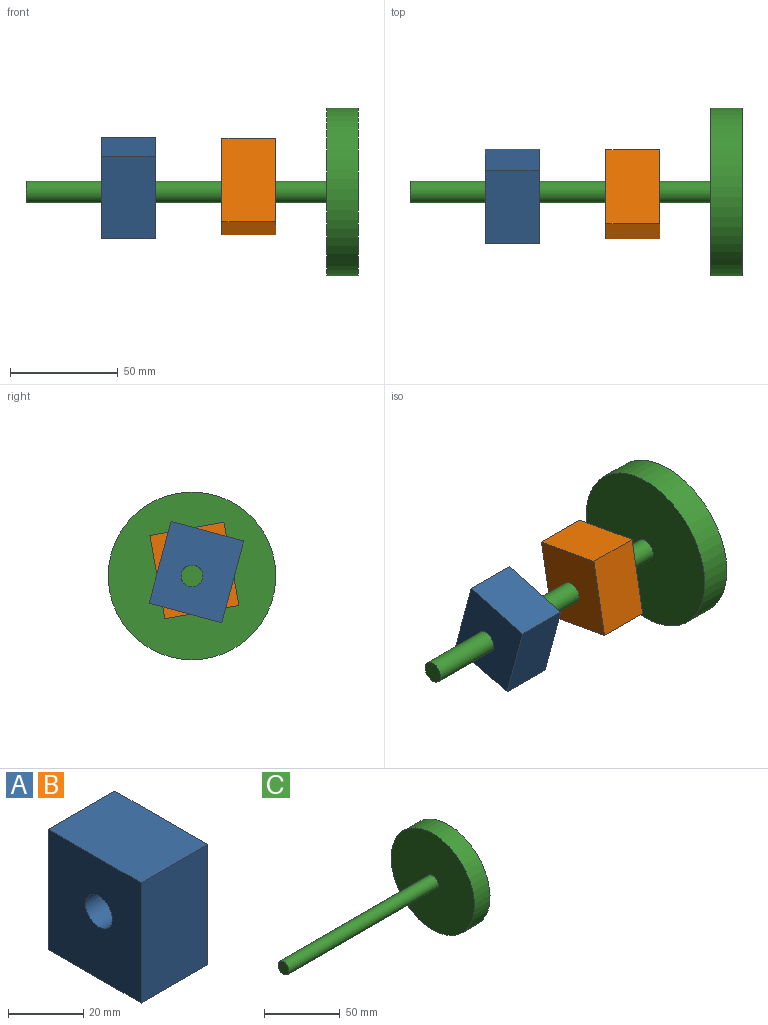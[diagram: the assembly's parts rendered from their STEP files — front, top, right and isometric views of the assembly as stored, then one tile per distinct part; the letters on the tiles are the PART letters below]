
ASSEMBLY  parts=3 mates=2
PART A: 7 faces, bbox 25x34.9x39.2 mm
  f0: plane 39.21x25mm, normal (0,-1,0), area 980.1mm2, adj f1,f3,f4,f5
  f1: plane 34.87x25mm, normal (0,0,-1), area 871.8mm2, adj f0,f2,f4,f5
  f2: plane 39.21x25mm, normal (0,1,0), area 980.1mm2, adj f1,f3,f4,f5
  f3: plane 34.87x25mm, normal (0,0,1), area 871.8mm2, adj f0,f2,f4,f5
  f4: plane 39.21x34.87mm, normal (1,0,0), area 1287.3mm2, adj f0,f1,f2,f3,f6
  f5: plane 39.21x34.87mm, normal (-1,0,0), area 1287.3mm2, adj f0,f1,f2,f3,f6
  f6: cylinder r=5.04mm len=25mm, axis (1,0,0), area 792.1mm2, adj f4,f5
PART B: same geometry as A
PART C: 5 faces, bbox 153.8x77.7x77.7 mm
  f0: cylinder r=5.04mm len=139.3mm, axis (1,0,0), area 4413.7mm2, adj f1,f3
  f1: plane 10.09x10.09mm, normal (-1,0,0), area 79.9mm2, adj f0
  f2: cylinder r=38.83mm len=77.67mm, axis (1,0,0), area 3538mm2, adj f3,f4
  f3: plane 77.67x77.67mm, normal (-1,0,0), area 4657.9mm2, adj f0,f2
  f4: plane 77.67x77.67mm, normal (1,0,0), area 4737.8mm2, adj f2
PLACE A rot(axis=(-1,0,0),165deg) t=(-19.79,24.79,122.27)mm
PLACE B rot(axis=(1,0,0),169.8deg) t=(36.12,34.62,115.73)mm
PLACE C t=(-2.73,-0.83,75.2)mm fixed
MATE cylindrical A.f6 <-> C.f0  axis (-1,0,0) through (-19.79,15.09,97.05)mm
MATE cylindrical C.f0 <-> B.f6  axis (1,0,0) through (15.02,15.09,97.05)mm
